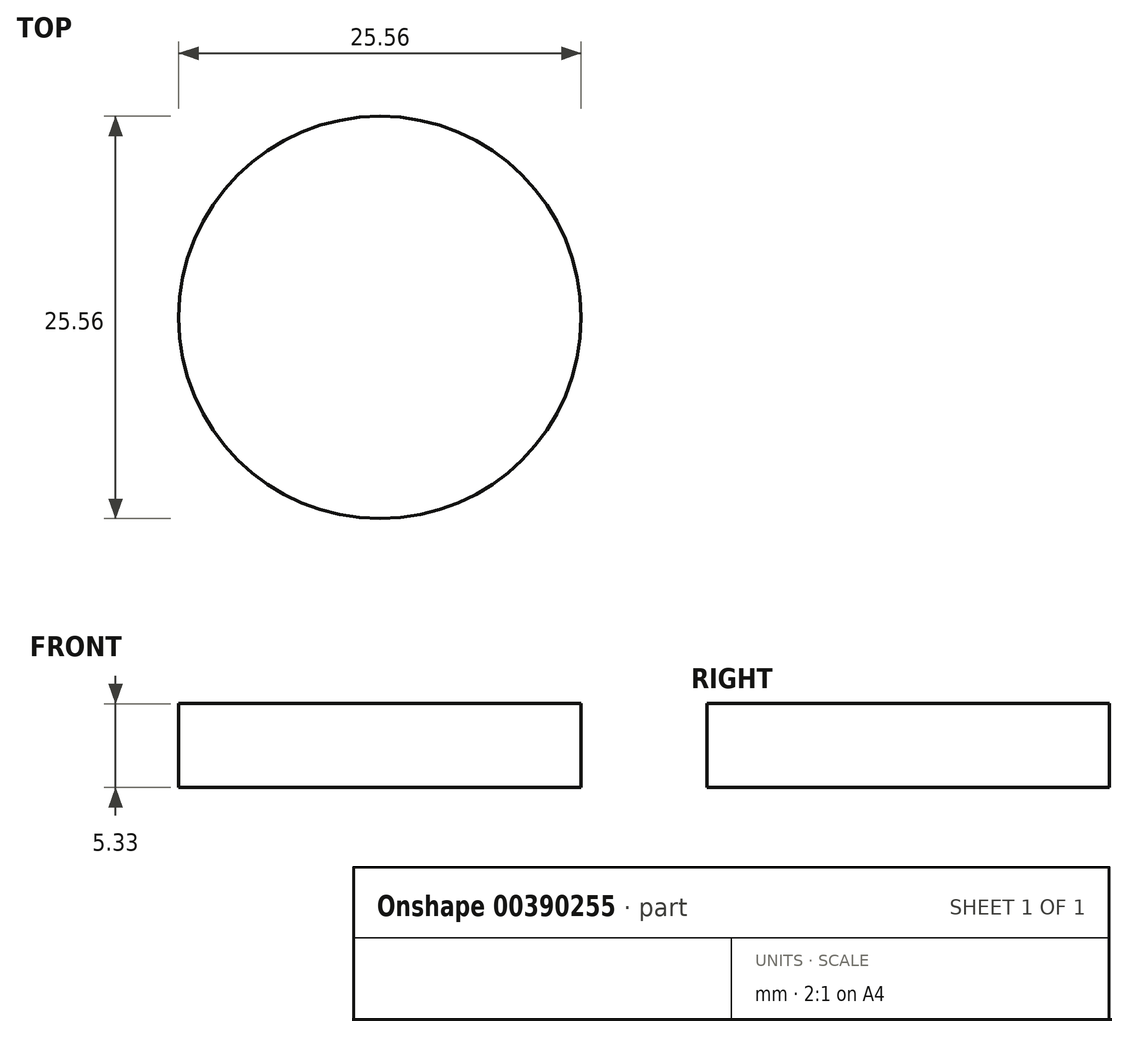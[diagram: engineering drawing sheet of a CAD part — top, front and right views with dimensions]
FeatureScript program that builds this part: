
annotation { "Feature Type Name" : "Feature", "Feature Type Description" : "" }
export const myFeature = defineFeature(function(context is Context, id is Id, definition is map)
    precondition{}
    {
        {
            var Q0;
            Q0=qCreatedBy(makeId("Top.planeOp"),FACE);
            var sketch = newSketch(context, id + "F0", { "sketchPlane" : qUnion([Q0])});
            skCircle(sketch, "E0", {"center": v(0, 0) * mm, "radius": 12.78 * mm});
            skSolve(sketch);
        }
        {
            var Q0;
            Q0 = qSketchRegion(id + "F0", true);
            extrude(context, id + "F1", {"entities" : qUnion([Q0]), "depth" : 5.33 * mm});
        }
    });
